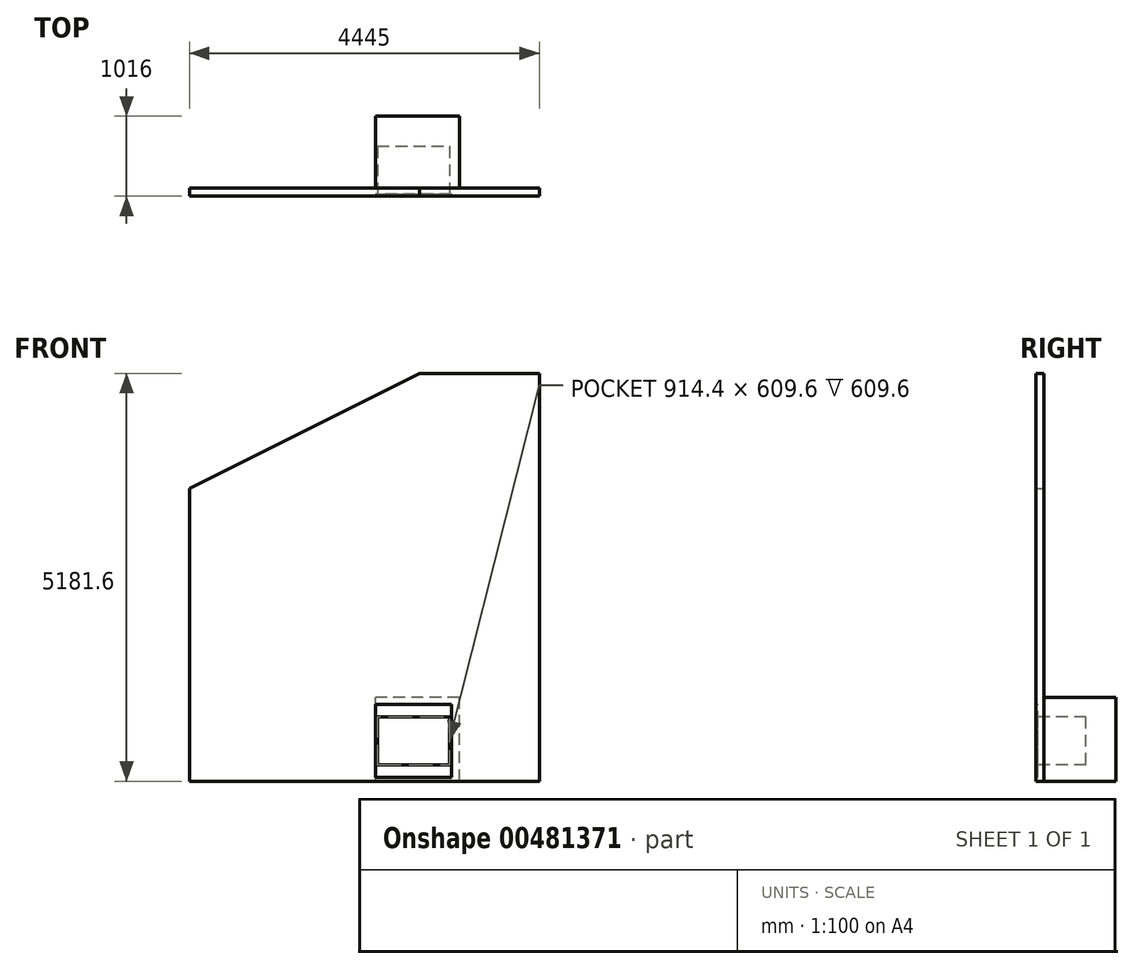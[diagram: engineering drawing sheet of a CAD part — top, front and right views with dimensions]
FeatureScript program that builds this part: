
annotation { "Feature Type Name" : "Feature", "Feature Type Description" : "" }
export const myFeature = defineFeature(function(context is Context, id is Id, definition is map)
    precondition{}
    {
        {
            var Q0;
            Q0=qCreatedBy(makeId("Front.planeOp"),FACE);
            var sketch = newSketch(context, id + "F0", { "sketchPlane" : qUnion([Q0])});
            skLineSegment(sketch, "E0.bottom", {"start": v(0, 0) * mm, "end": v(4445, 0) * mm});
            skLineSegment(sketch, "E1", {"start": v(4445, 0) * mm, "end": v(4445, 5181.6) * mm});
            skLineSegment(sketch, "E2", {"start": v(4445, 5181.6) * mm, "end": v(2921, 5181.6) * mm});
            skLineSegment(sketch, "E3", {"start": v(0, 0) * mm, "end": v(0, 3720.78) * mm});
            skLineSegment(sketch, "E4", {"start": v(0, 3720.78) * mm, "end": v(2921, 5181.6) * mm});
            skSolve(sketch);
        }
        {
            var Q0;
            Q0=makeQuery(id+"F0.imprint","IMPRINT",FACE,{"disambiguationData":[TD([[makeQuery(id+"F0.imprint","IMPRINT",EDGE,{"derivedFrom":sQuery(id+"F0.wireOp",EDGE,"E0.bottom")}),1.0]])]});
            extrude(context, id + "F1", {"entities" : qUnion([Q0]), "depth" : 101.6 * mm});
        }
        {
            var Q0;
            Q0=makeQuery(id+"F1.opExtrude","CAP_FACE",FACE,{"disambiguationData":[OSD([sQuery(id+"F0.wireOp",EDGE,"E0.bottom"),sQuery(id+"F0.wireOp",EDGE,"E1"),sQuery(id+"F0.wireOp",EDGE,"E2"),sQuery(id+"F0.wireOp",EDGE,"E3"),sQuery(id+"F0.wireOp",EDGE,"E4")])],"isStart":false});
            var sketch = newSketch(context, id + "F2", { "sketchPlane" : qUnion([Q0])});
            skLineSegment(sketch, "E5.bottom", {"start": v(3429, 0) * mm, "end": v(2362.2, 0) * mm});
            skLineSegment(sketch, "E5.top", {"start": v(3429, 1066.8) * mm, "end": v(2362.2, 1066.8) * mm});
            skLineSegment(sketch, "E5.left", {"start": v(3429, 0) * mm, "end": v(3429, 1066.8) * mm});
            skLineSegment(sketch, "E5.right", {"start": v(2362.2, 0) * mm, "end": v(2362.2, 1066.8) * mm});
            skSolve(sketch);
        }
        {
            var Q0;
            Q0=makeQuery(id+"F2.imprint","IMPRINT",FACE,{"disambiguationData":[TD([[makeQuery(id+"F2.imprint","IMPRINT",EDGE,{"derivedFrom":sQuery(id+"F2.wireOp",EDGE,"E5.bottom")}),1.0]])]});
            extrude(context, id + "F3", {"entities" : qUnion([Q0]), "operationType" : NewBodyOperationType.ADD, "oppositeDirection" : true, "depth" : 1016 * mm});
        }
        {
            var Q0;
            Q0=makeQuery(id+"F1.opExtrude","CAP_FACE",FACE,{"disambiguationData":[OSD([sQuery(id+"F0.wireOp",EDGE,"E0.bottom"),sQuery(id+"F0.wireOp",EDGE,"E1"),sQuery(id+"F0.wireOp",EDGE,"E2"),sQuery(id+"F0.wireOp",EDGE,"E3"),sQuery(id+"F0.wireOp",EDGE,"E4")])],"isStart":false});
            var sketch = newSketch(context, id + "F4", { "sketchPlane" : qUnion([Q0])});
            skLineSegment(sketch, "E6.bottom", {"start": v(3327.4, 50.8) * mm, "end": v(2362.2, 50.8) * mm});
            skLineSegment(sketch, "E6.top", {"start": v(3327.4, 977.9) * mm, "end": v(2362.2, 977.9) * mm});
            skLineSegment(sketch, "E6.left", {"start": v(3327.4, 50.8) * mm, "end": v(3327.4, 977.9) * mm});
            skLineSegment(sketch, "E6.right", {"start": v(2362.2, 50.8) * mm, "end": v(2362.2, 977.9) * mm});
            skSolve(sketch);
        }
        {
            var Q0;
            Q0=makeQuery(id+"F4.imprint","IMPRINT",FACE,{"disambiguationData":[TD([[makeQuery(id+"F4.imprint","IMPRINT",EDGE,{"derivedFrom":sQuery(id+"F4.wireOp",EDGE,"E6.bottom")}),-1.0]])]});
            extrude(context, id + "F5", {"entities" : qUnion([Q0]), "operationType" : NewBodyOperationType.REMOVE, "oppositeDirection" : true, "depth" : 25.4 * mm});
        }
        {
            var Q0;
            Q0=makeQuery(id+"F5.boolean.opBoolean","COPY",FACE,{"derivedFrom":makeQuery(id+"F5.opExtrude","CAP_FACE",FACE,{"disambiguationData":[OSD([sQuery(id+"F4.wireOp",EDGE,"E6.bottom"),sQuery(id+"F4.wireOp",EDGE,"E6.top"),sQuery(id+"F4.wireOp",EDGE,"E6.left"),sQuery(id+"F4.wireOp",EDGE,"E6.right")])],"isStart":false})});
            var sketch = newSketch(context, id + "F6", { "sketchPlane" : qUnion([Q0])});
            skLineSegment(sketch, "E7.bottom", {"start": v(2387.6, 209.55) * mm, "end": v(3302, 209.55) * mm});
            skLineSegment(sketch, "E7.top", {"start": v(2387.6, 819.15) * mm, "end": v(3302, 819.15) * mm});
            skLineSegment(sketch, "E7.left", {"start": v(2387.6, 209.55) * mm, "end": v(2387.6, 819.15) * mm});
            skLineSegment(sketch, "E7.right", {"start": v(3302, 209.55) * mm, "end": v(3302, 819.15) * mm});
            skSolve(sketch);
        }
        {
            var Q0;
            Q0=makeQuery(id+"F6.imprint","IMPRINT",FACE,{"disambiguationData":[TD([[makeQuery(id+"F6.imprint","IMPRINT",EDGE,{"derivedFrom":sQuery(id+"F6.wireOp",EDGE,"E7.bottom")}),1.0]])]});
            extrude(context, id + "F7", {"entities" : qUnion([Q0]), "operationType" : NewBodyOperationType.REMOVE, "oppositeDirection" : true, "depth" : 609.6 * mm});
        }
    });
